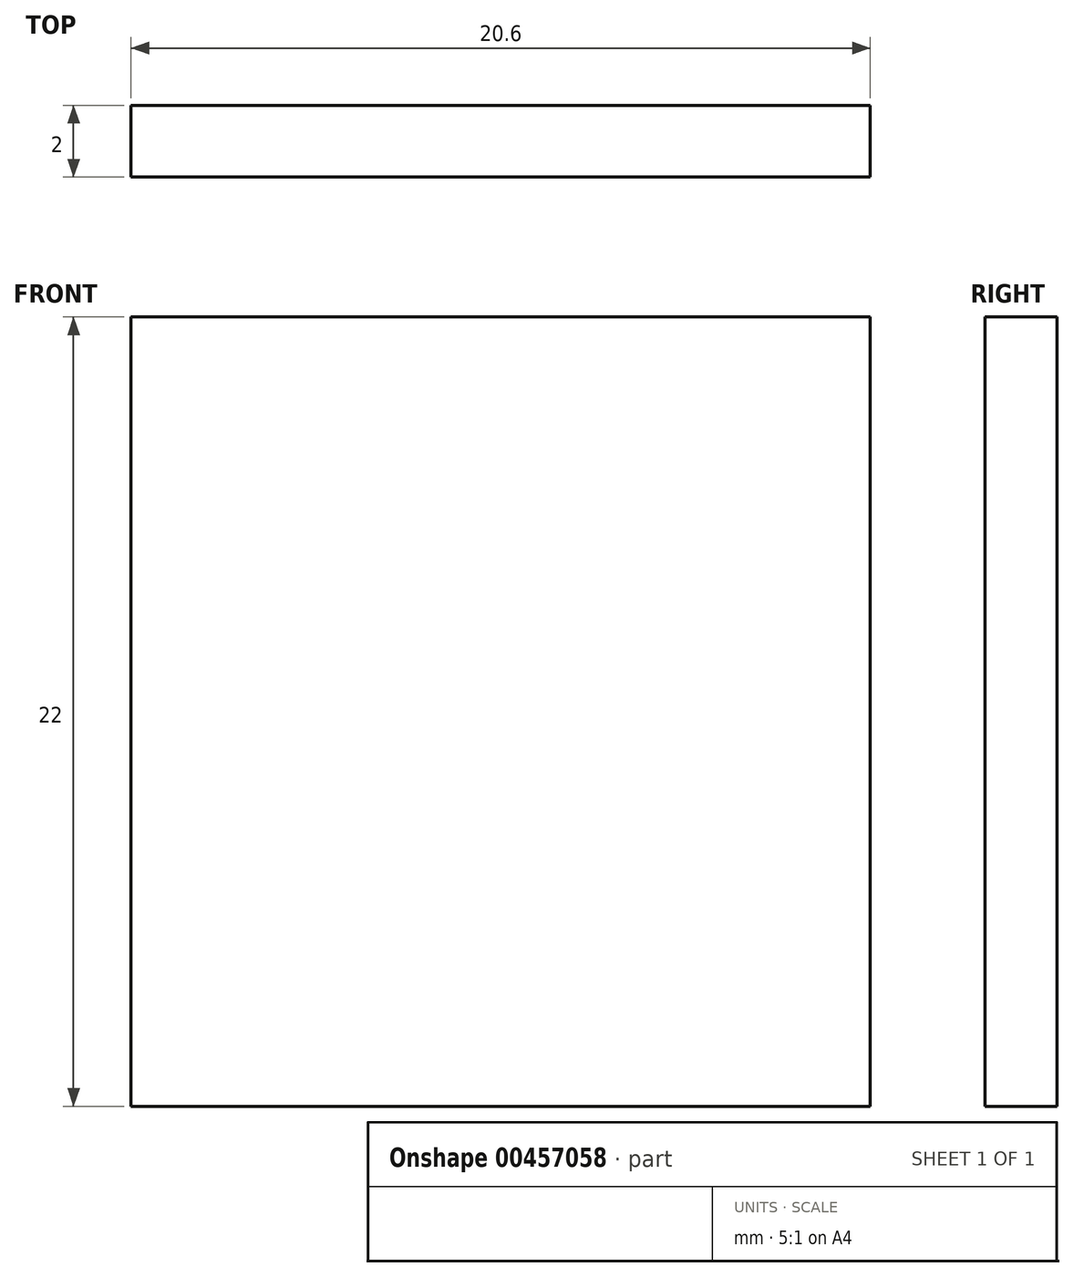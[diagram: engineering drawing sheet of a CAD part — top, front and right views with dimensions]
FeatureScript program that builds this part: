
annotation { "Feature Type Name" : "Feature", "Feature Type Description" : "" }
export const myFeature = defineFeature(function(context is Context, id is Id, definition is map)
    precondition{}
    {
        {
            var Q0;
            Q0=qCreatedBy(makeId("Front.planeOp"),FACE);
            var sketch = newSketch(context, id + "F0", { "sketchPlane" : qUnion([Q0])});
            skLineSegment(sketch, "E0.bottom", {"start": v(-25.22, 33.88) * mm, "end": v(-4.62, 33.88) * mm});
            skLineSegment(sketch, "E0.top", {"start": v(-25.22, 11.88) * mm, "end": v(-4.62, 11.88) * mm});
            skLineSegment(sketch, "E0.left", {"start": v(-25.22, 33.88) * mm, "end": v(-25.22, 11.88) * mm});
            skLineSegment(sketch, "E0.right", {"start": v(-4.62, 33.88) * mm, "end": v(-4.62, 11.88) * mm});
            skSolve(sketch);
        }
        {
            var Q0;
            Q0 = qSketchRegion(id + "F0", true);
            extrude(context, id + "F1", {"entities" : qUnion([Q0]), "depth" : 2 * mm});
        }
    });
